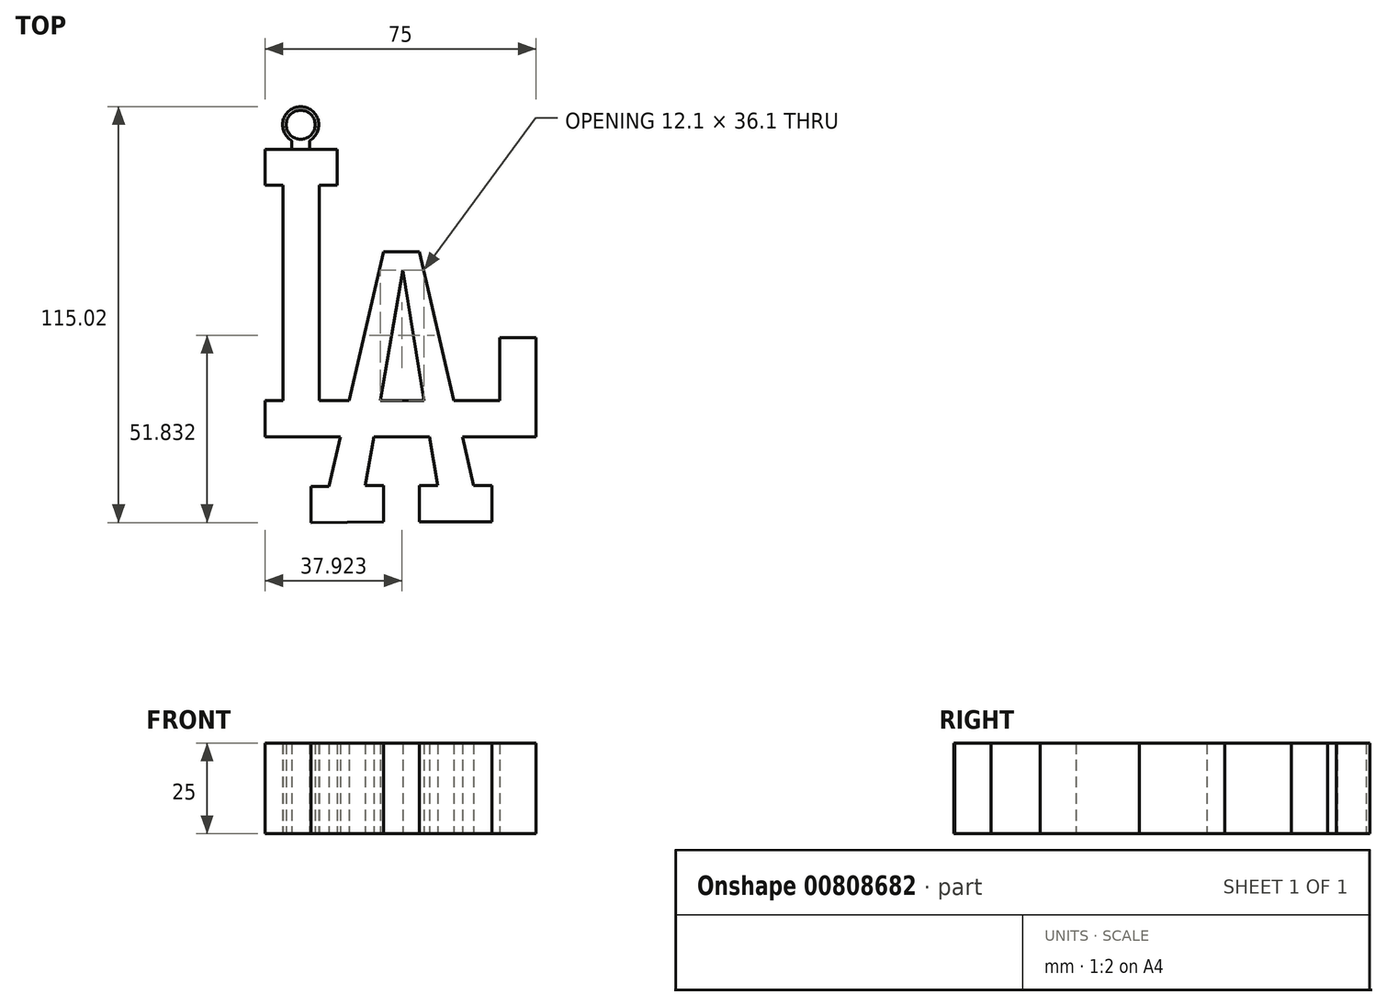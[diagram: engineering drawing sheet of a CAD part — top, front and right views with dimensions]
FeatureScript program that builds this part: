
annotation { "Feature Type Name" : "Feature", "Feature Type Description" : "" }
export const myFeature = defineFeature(function(context is Context, id is Id, definition is map)
    precondition{}
    {
        {
            var Q0;
            Q0=qCreatedBy(makeId("Top.planeOp"),FACE);
            var sketch = newSketch(context, id + "F0", { "sketchPlane" : qUnion([Q0])});
            skLineSegment(sketch, "E0", {"start": v(-47.75, 69.1) * mm, "end": v(-27.75, 69.1) * mm});
            skLineSegment(sketch, "E1", {"start": v(-27.75, 69.1) * mm, "end": v(-27.75, 59.1) * mm});
            skLineSegment(sketch, "E2", {"start": v(-27.75, 59.1) * mm, "end": v(-32.75, 59.1) * mm});
            skLineSegment(sketch, "E3", {"start": v(-32.75, 59.1) * mm, "end": v(-32.75, -0.4) * mm});
            skLineSegment(sketch, "E4", {"start": v(-32.75, -0.4) * mm, "end": v(17.25, -0.4) * mm});
            skLineSegment(sketch, "E5", {"start": v(17.25, -0.4) * mm, "end": v(17.25, 17.03) * mm});
            skLineSegment(sketch, "E6", {"start": v(17.25, 17.03) * mm, "end": v(27.25, 17.03) * mm});
            skLineSegment(sketch, "E7", {"start": v(27.25, 17.03) * mm, "end": v(27.25, -10.4) * mm});
            skLineSegment(sketch, "E8", {"start": v(27.25, -10.4) * mm, "end": v(-47.75, -10.4) * mm});
            skLineSegment(sketch, "E9", {"start": v(-47.75, -10.4) * mm, "end": v(-47.75, -0.4) * mm});
            skLineSegment(sketch, "E10", {"start": v(-47.75, -0.4) * mm, "end": v(-42.75, -0.4) * mm});
            skLineSegment(sketch, "E11", {"start": v(-42.75, -0.4) * mm, "end": v(-42.75, 59.1) * mm});
            skLineSegment(sketch, "E12", {"start": v(-42.75, 59.1) * mm, "end": v(-47.75, 59.1) * mm});
            skLineSegment(sketch, "E13", {"start": v(-47.75, 59.1) * mm, "end": v(-47.75, 69.1) * mm});
            skLineSegment(sketch, "E14", {"start": v(-35, -34.18) * mm, "end": v(-35, -24.18) * mm});
            skLineSegment(sketch, "E15", {"start": v(-35, -24.18) * mm, "end": v(-30, -24.18) * mm});
            skLineSegment(sketch, "E16", {"start": v(-30, -24.18) * mm, "end": v(-15, 40.7) * mm});
            skLineSegment(sketch, "E17", {"start": v(-15, 40.7) * mm, "end": v(-5, 40.7) * mm});
            skLineSegment(sketch, "E18", {"start": v(-5, 40.7) * mm, "end": v(10, -23.97) * mm});
            skLineSegment(sketch, "E19", {"start": v(10, -23.97) * mm, "end": v(15, -23.97) * mm});
            skLineSegment(sketch, "E20", {"start": v(15, -23.97) * mm, "end": v(15, -33.97) * mm});
            skLineSegment(sketch, "E21", {"start": v(15, -33.97) * mm, "end": v(-5, -33.97) * mm});
            skLineSegment(sketch, "E22", {"start": v(-5, -33.97) * mm, "end": v(-5, -23.97) * mm});
            skLineSegment(sketch, "E23", {"start": v(-5, -23.97) * mm, "end": v(0, -23.97) * mm});
            skLineSegment(sketch, "E24", {"start": v(-20, -23.97) * mm, "end": v(-15, -23.97) * mm});
            skLineSegment(sketch, "E25", {"start": v(-15, -23.97) * mm, "end": v(-15, -33.97) * mm});
            skLineSegment(sketch, "E26", {"start": v(-15, -33.97) * mm, "end": v(-35, -34.18) * mm});
            skLineSegment(sketch, "E27", {"start": v(-20, -23.97) * mm, "end": v(-9.56, 35.7) * mm});
            skLineSegment(sketch, "E28", {"start": v(-9.56, 35.7) * mm, "end": v(0, -23.97) * mm});
            skSolve(sketch);
        }
        {
            var Q0;
            Q0=qCreatedBy(makeId("Top.planeOp"),FACE);
            var sketch = newSketch(context, id + "F1", { "sketchPlane" : qUnion([Q0])});
            skLineSegment(sketch, "E29", {"start": v(-40.35, 69.1) * mm, "end": v(-40.35, 71.51) * mm});
            skArc(sketch, "E30", {"start": v(-35.35, 71.51) * mm, "mid": v(-37.85, 80.84) * mm, "end": v(-40.35, 71.51) * mm});
            skLineSegment(sketch, "E31", {"start": v(-35.35, 71.51) * mm, "end": v(-35.35, 69.12) * mm});
            skLineSegment(sketch, "E32", {"start": v(-40.35, 69.1) * mm, "end": v(-35.35, 69.12) * mm});
            skSolve(sketch);
        }
        {
            var Q0;
            Q0 = qSketchRegion(id + "F0", true);
            var Q1;
            Q1 = qSketchRegion(id + "F1", true);
            extrude(context, id + "F2", {"entities" : qUnion([Q0, Q1]), "depth" : 25 * mm, "offsetDistance" : 25 * mm});
        }
        {
            var Q0;
            Q0 = qSketchRegion(id + "F1", true);
            extrude(context, id + "F3", {"entities" : qUnion([Q0]), "depth" : 25 * mm, "offsetDistance" : 25 * mm});
        }
        {
            var Q0;
            Q0=qCreatedBy(makeId("Top.planeOp"),FACE);
            var sketch = newSketch(context, id + "F4", { "sketchPlane" : qUnion([Q0])});
            skCircle(sketch, "E33", {"center": v(-37.86, 75.84) * mm, "radius": 4 * mm});
            skSolve(sketch);
        }
        {
            var Q0;
            Q0 = qSketchRegion(id + "F4", true);
            extrude(context, id + "F5", {"entities" : qUnion([Q0]), "depth" : 25 * mm, "offsetDistance" : 25 * mm});
        }
    });
